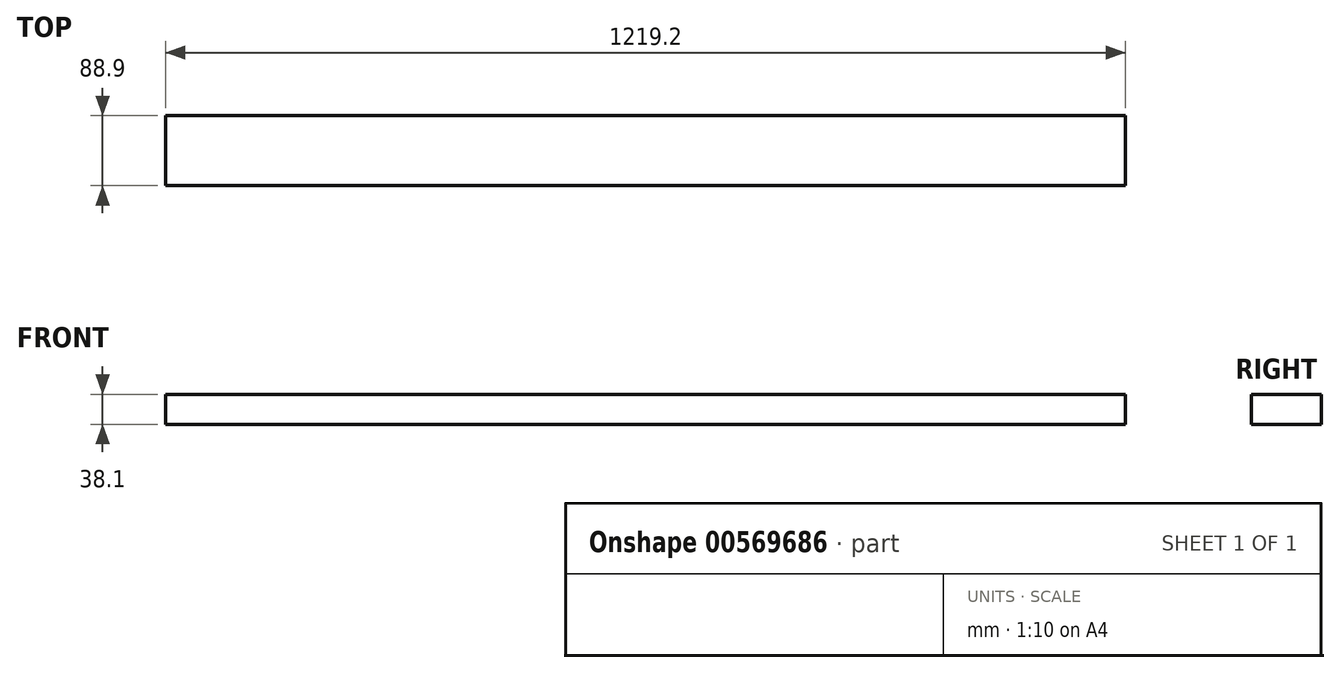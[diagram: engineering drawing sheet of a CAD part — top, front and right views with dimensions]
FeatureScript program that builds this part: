
annotation { "Feature Type Name" : "Feature", "Feature Type Description" : "" }
export const myFeature = defineFeature(function(context is Context, id is Id, definition is map)
    precondition{}
    {
        {
            var Q0;
            Q0=qCreatedBy(makeId("Front.planeOp"),FACE);
            var sketch = newSketch(context, id + "F0", { "sketchPlane" : qUnion([Q0])});
            skLineSegment(sketch, "E0", {"start": v(0, 0) * mm, "end": v(0, -38.1) * mm});
            skLineSegment(sketch, "E1", {"start": v(0, -38.1) * mm, "end": v(1219.2, -38.1) * mm});
            skLineSegment(sketch, "E2", {"start": v(1219.2, -38.1) * mm, "end": v(1219.2, 0) * mm});
            skLineSegment(sketch, "E3", {"start": v(1219.2, 0) * mm, "end": v(0, 0) * mm});
            skSolve(sketch);
        }
        {
            var Q0;
            Q0 = qSketchRegion(id + "F0", true);
            extrude(context, id + "F1", {"entities" : qUnion([Q0]), "depth" : 88.9 * mm, "offsetDistance" : 25.4 * mm});
        }
    });
